# Revit family: DonoBrace
name_source: partatom
category: Structural Connections
units: mm (PartAtom-declared; Revit-internal decimal feet)

## family parameters
Cut with Voids When Loaded = No
Enable cutting in views = Yes
Material for Model Behavior = Other
Shared = No

## types (6) — shared parameters
zero-valued in all types: Default Elevation

## per-type parameters (varying)
| type | Coupler_DB15EC | Coupler_DB20EC | Coupler_DB25EC | DB15EC Vis | DB20EC Vis | DB25EC Vis | Rod Cutback | Tie Rod Radius |
| DB15EC | No | No | No | Yes | No | No | 55 mm | 8 mm  [stored 0.0262467 ft] |
| DB20EC | No | No | No | No | Yes | No | 75 mm | 10 mm  [stored 0.0328084 ft] |
| DB25EC | No | No | No | No | No | Yes | 110 mm  [stored 0.360892 ft] | 13 mm  [stored 0.0426509 ft] |
| DB15EC_Coupler | Yes | No | No | Yes | No | No | 55 mm | 8 mm  [stored 0.0262467 ft] |
| DB20EC_Coupler | No | Yes | No | No | Yes | No | 75 mm | 10 mm  [stored 0.0328084 ft] |
| DB25EC_Coupler | No | No | Yes | No | No | Yes | 110 mm  [stored 0.360892 ft] | 13 mm  [stored 0.0426509 ft] |

note: [stored X ft] marks values corroborated as IEEE doubles in the binary element streams (Revit-internal decimal feet)

## geometry (parser evidence)
native form markers: Sweep x40
no freeform markers — native parametric forms only
